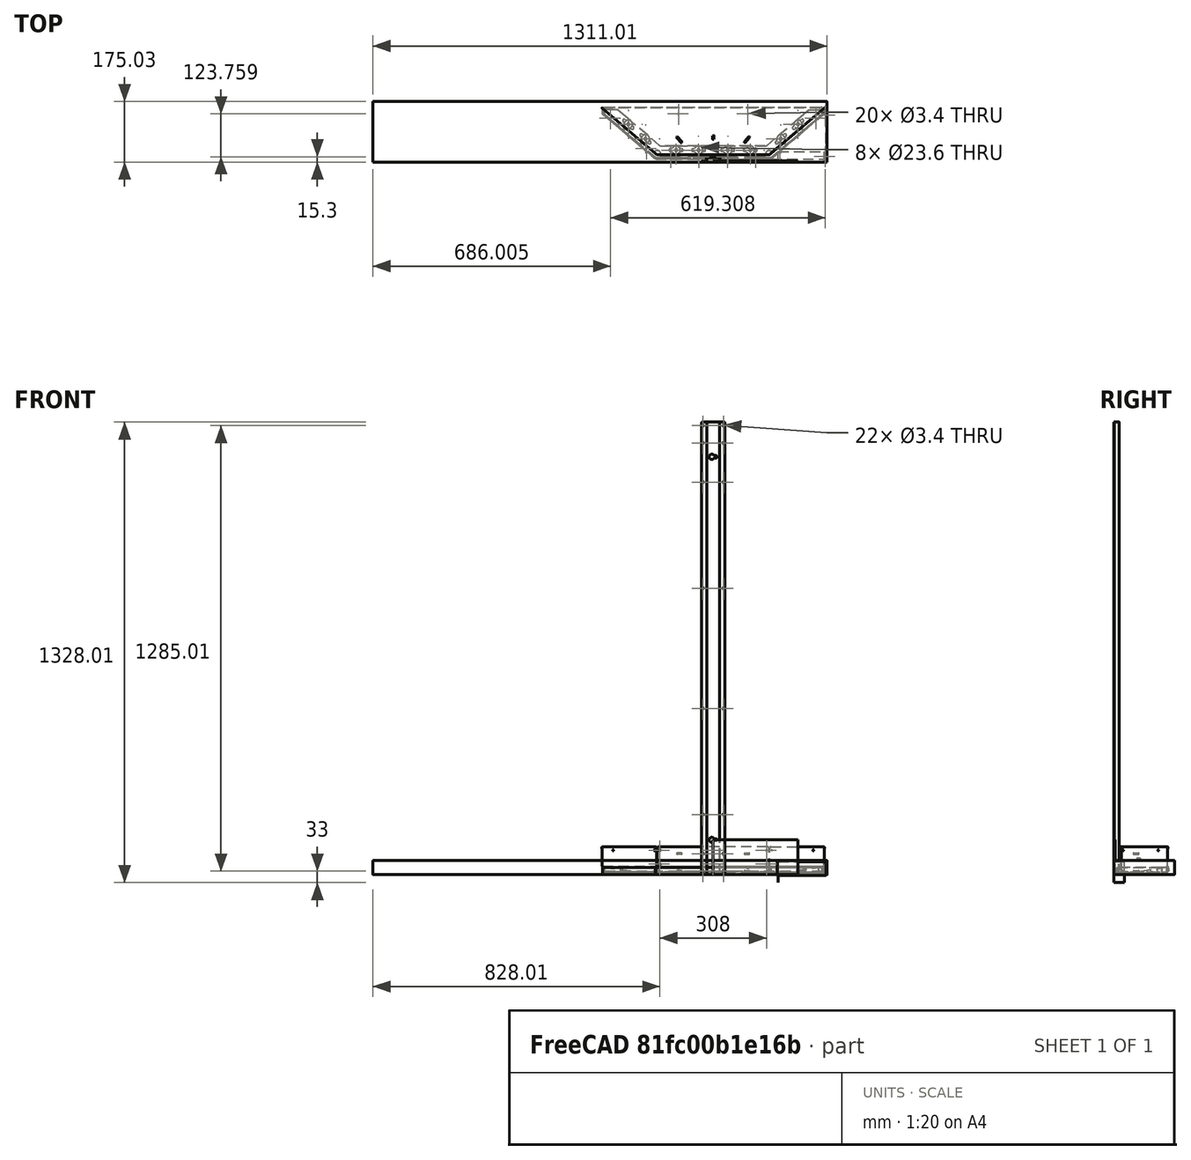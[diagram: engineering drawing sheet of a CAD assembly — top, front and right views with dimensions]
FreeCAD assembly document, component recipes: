
FREECAD ASSEMBLY — COMPONENT RECIPES ("composit_stand7")

This assembly document has 10 components, labeled P0..P9 below (a component is one placed body or linked part). 10 of them carry a construction recipe — the FreeCAD feature program that regenerates the part from scratch, quoted from this document or its linked companion documents; the rest are supplied as boundary geometry only. No exploded tour is included for this assembly.
COMPONENT P0 — recipe-attached ("Body006", modeled in this document).
Construction recipe (the document's own serialized feature program — sketch geometry with constraints, then the solid features built on it; lengths are millimeters unless a unit is written):

FEATURE [PartDesign::SubShapeBinder] Binder011
  BindCopyOnChange = 0
  BindMode = 0
  ClaimChildren = true
  Context = -> Part [Part001.Body005.Boolean003.Body006.Binder011.]
  Fuse = false
  MakeFace = true
  OffsetFill = false
  OffsetIntersection = false
  OffsetJoinType = 0
  OffsetOpenResult = false
  PartialLoad = false
  Relative = false
  Support = -> [Sketch019]
  _Version = 2
FEATURE [PartDesign::FeaturePython] BaseBend004  # WARN: FeaturePython — macro-defined, semantics opaque (R4)
  BendSide = 1
  BendSketch = -> Binder011
  MidPlane = false
  Reverse = true
  length = 10
  radius = 0.1
  thickness = 0.3
FEATURE [PartDesign::Plane] DatumPlane
  AttachmentOffset = pos=(0,0,-326.502) rot=(0,0,1;0rad)
  Length = 220.036
  MapMode = 5
  Placement = pos=(-326.502,0,0) rot=(0.57735,0.57735,0.57735;2.0944rad)
  ResizeMode = 0
  Support = -> [YZ_Plane008]
  Width = 70.0017
  expr: .AttachmentOffset.Base.z = <<faces_bridge>>.Constraints.offset
FEATURE [PartDesign::CoordinateSystem] Local_CS
  AttacherType = Attacher::AttachEngine3D
  AttachmentOffset = pos=(0,0,0) rot=(0,1,0;1.5708rad)
  MapMode = 7
  Placement = pos=(329.002,156.059,0) rot=(0.57735,0.57735,0.57735;2.0944rad)
  Support = -> [Binder011]
FEATURE [Sketcher::SketchObject] Sketch020
  FullyConstrained = true
  MapMode = 5
  Placement = pos=(329.002,156.059,0) rot=(0.57735,0.57735,0.57735;2.0944rad)
  Support = -> [Local_CS]
  expr: Constraints[6] = -<<BaseBend004>>.length
  sketch-geometry (3):
    g0: ArcOfCircle CenterX=5 CenterY=-5 CenterZ=0 NormalX=0 NormalY=0 NormalZ=1 AngleXU=0 Radius=5 StartAngle=3.14159 EndAngle=4.71239
    g1: LineSegment StartX=0 StartY=-5 StartZ=0 EndX=0 EndY=-10 EndZ=0
    g2: LineSegment StartX=0 StartY=-10 StartZ=0 EndX=5 EndY=-10 EndZ=0
  constraints (8):
    c: PointOnObject(g0,g-2)
    c: PointOnObject(g1,g-2)
    c: Coincident(g2,g1)
    c: Horizontal(g2)
    c: Tangent(g2,g0) = -1.5708
    c: Tangent(g1,g0) = -1.5708
    c: DistanceY(g1) = -10
    c: DistanceX(g2,g2) = 5
FEATURE [PartDesign::Pocket] Pocket002
  BaseFeature = -> BaseBend004
  Direction = (-1,0,0)
  Length = 5
  Length2 = 5
  Profile = -> Sketch020
  ReferenceAxis = -> Sketch020 [N_Axis]
  Type = 0
FEATURE [PartDesign::Mirrored] Mirrored002
  BaseFeature = -> Pocket002
  MirrorPlane = -> DatumPlane
  Originals = -> [Pocket002]
FEATURE [PartDesign::Body] Body006
  Group = -> [Binder011,BaseBend004,DatumPlane,Local_CS,Sketch020,Pocket002,Mirrored002]
  Origin = -> Origin008
  Tip = -> Mirrored002
COMPONENT P1 — recipe-attached ("sink2_material_0.30ansi", modeled in this document).
Construction recipe (the document's own serialized feature program — sketch geometry with constraints, then the solid features built on it; lengths are millimeters unless a unit is written):

FEATURE [PartDesign::SubShapeBinder] Binder016
  BindCopyOnChange = 0
  BindMode = 0
  ClaimChildren = true
  Context = -> Body011 [Binder016.]
  Fuse = false
  MakeFace = true
  OffsetFill = false
  OffsetIntersection = false
  OffsetJoinType = 0
  OffsetOpenResult = false
  PartialLoad = false
  Placement = pos=(0,0,0) rot=(1,0,0;1.5708rad)
  Relative = false
  Support = -> [Sketch049]
  _Version = 2
FEATURE [PartDesign::Pad] Pad014
  Direction = (0,-1,2e-16)
  Length = 1
  Length2 = 10
  Placement = pos=(0,0,0) rot=(1,0,0;1.5708rad)
  Profile = -> Binder016
  Reversed = true
  Type = 0
FEATURE [PartDesign::FeaturePython] Bend004  # WARN: FeaturePython — macro-defined, semantics opaque (R4)
  AutoMiter = true
  BaseFeature = -> Pad014
  BendType = 0
  LengthList = [50]
  LengthSpec = 0
  ReliefFactor = 0.7
  UseReliefFactor = false
  angle = 40
  baseObject = -> Pad014 [Edge3]
  bendAList = [40]
  extend1 = 0
  extend2 = 0
  gap1 = 0
  gap2 = 0
  invert = false
  kfactor = 0.5
  length = 50
  maxExtendDist = 5
  minGap = 0.1
  minReliefGap = 1
  miterangle1 = 0
  miterangle2 = 0
  offset = 0
  radius = 1
  reliefType = 0
  reliefd = 1
  reliefw = 0.8
  sketchflip = false
  sketchinvert = false
  unfold = false
FEATURE [Sketcher::SketchObject] Sketch062
  ExternalGeometry = -> [Bend004]
  FullyConstrained = true
  MapMode = 5
  Placement = pos=(0,0.407604,0.34202) rot=(0,0.422618,0.906308;3.14159rad)
  Support = -> [Bend004]
  sketch-geometry (3):
    g0: LineSegment StartX=325.502 StartY=-51.2856 StartZ=0 EndX=-193.217 EndY=-24.1006 EndZ=0
    g1: LineSegment StartX=-193.217 StartY=-24.1006 StartZ=0 EndX=-193.217 EndY=-51.2856 EndZ=0
    g2: LineSegment StartX=-193.217 StartY=-51.2856 StartZ=0 EndX=325.502 EndY=-51.2856 EndZ=0
  constraints (7):
    c: Coincident(g0,g1)
    c: Vertical(g1)
    c: Angle(g0) = 3.08923
    c: Coincident(g0,g-4)
    c: Coincident(g1,g-4)
    c: Coincident(g2,g1)
    c: Coincident(g2,g0)
FEATURE [PartDesign::Pocket] Pocket012
  BaseFeature = -> Bend004
  Direction = (0,-0.766044,-0.642788)
  Length = 5
  Length2 = 5
  Profile = -> Sketch062
  ReferenceAxis = -> Sketch062 [N_Axis]
  Type = 0
FEATURE [PartDesign::FeaturePython] Bend005  # WARN: FeaturePython — macro-defined, semantics opaque (R4)
  AutoMiter = true
  BaseFeature = -> Pocket012
  BendType = 0
  LengthList = [20]
  LengthSpec = 0
  ReliefFactor = 0.7
  UseReliefFactor = false
  angle = 90
  baseObject = -> Pocket012 [Edge10]
  bendAList = [90]
  extend1 = 0
  extend2 = 0
  gap1 = 0
  gap2 = 0
  invert = false
  kfactor = 0.5
  length = 20
  maxExtendDist = 5
  minGap = 0.1
  minReliefGap = 1
  miterangle1 = 0
  miterangle2 = 0
  offset = 0
  radius = 1
  reliefType = 0
  reliefd = 1
  reliefw = 0.8
  sketchflip = false
  sketchinvert = false
  unfold = false
  expr: radius = Bend004.radius
FEATURE [PartDesign::Boolean] Boolean014
  BaseFeature = -> Bend005
  Group = -> [Compound025]
  Type = 1
FEATURE [PartDesign::Fillet] Fillet002
  Base = -> Boolean014 [Edge36,Edge2,Edge8,Edge50]
  BaseFeature = -> Boolean014
  Radius = 11
  SupportTransform = false
  UseAllEdges = false
FEATURE [PartDesign::Body] Body011  label="sink2_material_0.30ansi"
  Group = -> [Binder016,Pad014,Bend004,Sketch062,Pocket012,Bend005,Boolean014,Fillet002]
  Origin = -> Origin014
  Placement = pos=(0,17,0) rot=(0,0,1;0rad)
  Tip = -> Fillet002
  expr: .Placement.Base.y = <<base_sketch>>.Constraints.offset - 3 mm - 1 mm
COMPONENT P2 — recipe-attached ("drain_holder", modeled in this document).
Construction recipe (the document's own serialized feature program — sketch geometry with constraints, then the solid features built on it; lengths are millimeters unless a unit is written):

FEATURE [PartDesign::SubShapeBinder] Binder017
  BindCopyOnChange = 0
  BindMode = 0
  ClaimChildren = true
  Context = -> Body012 [Binder017.]
  Fuse = false
  MakeFace = true
  OffsetFill = false
  OffsetIntersection = false
  OffsetJoinType = 0
  OffsetOpenResult = false
  PartialLoad = false
  Relative = false
  Support = -> [Sketch050]
  _Version = 2
FEATURE [PartDesign::FeaturePython] BaseBend007  # WARN: FeaturePython — macro-defined, semantics opaque (R4)
  BendSide = 0
  BendSketch = -> Binder017
  MidPlane = false
  Reverse = false
  length = 70
  radius = 0.1
  thickness = 0.3
FEATURE [PartDesign::Boolean] Boolean008
  BaseFeature = -> BaseBend007
  Group = -> [Compound018]
  Type = 1
FEATURE [PartDesign::Body] Body012  label="drain_holder"
  Group = -> [Binder017,BaseBend007,Boolean008]
  Origin = -> Origin015
  Placement = pos=(-313,0,-115) rot=(0,0,1;0rad)
  Tip = -> Boolean008
COMPONENT P3 — recipe-attached ("front_shield", modeled in this document).
Construction recipe (the document's own serialized feature program — sketch geometry with constraints, then the solid features built on it; lengths are millimeters unless a unit is written):

FEATURE [PartDesign::SubShapeBinder] Binder020
  BindCopyOnChange = 0
  BindMode = 0
  ClaimChildren = true
  Context = -> Body013 [Binder020.]
  Fuse = false
  MakeFace = true
  OffsetFill = false
  OffsetIntersection = false
  OffsetJoinType = 0
  OffsetOpenResult = false
  PartialLoad = false
  Relative = false
  Support = -> [Sketch057]
  _Version = 2
FEATURE [PartDesign::FeaturePython] BaseBend008  # WARN: FeaturePython — macro-defined, semantics opaque (R4)
  BendSide = 0
  BendSketch = -> Binder020
  MidPlane = false
  Reverse = false
  length = 133
  radius = 0
  thickness = 0.3
  expr: length = <<Properties>>.bottom_extend + 18 mm
FEATURE [PartDesign::Boolean] Boolean009
  BaseFeature = -> BaseBend008
  Group = -> [Compound017]
  Type = 1
FEATURE [PartDesign::Body] Body013  label="front_shield"
  Group = -> [Binder020,BaseBend008,Boolean009]
  Origin = -> Origin016
  Placement = pos=(0,154.059,-115) rot=(0,0,1;0rad)
  Tip = -> Boolean009
  expr: Placement = <<front_shield_placement>>.Placement
COMPONENT P4 — recipe-attached ("led_holder", modeled in this document).
Construction recipe (the document's own serialized feature program — sketch geometry with constraints, then the solid features built on it; lengths are millimeters unless a unit is written):

FEATURE [PartDesign::SubShapeBinder] Binder023
  BindCopyOnChange = 0
  BindMode = 0
  ClaimChildren = true
  Context = -> Body015 [Binder023.]
  Fuse = false
  MakeFace = true
  OffsetFill = false
  OffsetIntersection = false
  OffsetJoinType = 0
  OffsetOpenResult = false
  PartialLoad = false
  Relative = true
  Support = -> [Sketch060]
  _Version = 2
FEATURE [PartDesign::SubShapeBinder] Binder024
  BindCopyOnChange = 0
  BindMode = 0
  ClaimChildren = true
  Context = -> Body015 [Binder024.]
  Fuse = false
  MakeFace = true
  OffsetFill = false
  OffsetIntersection = false
  OffsetJoinType = 0
  OffsetOpenResult = false
  PartialLoad = false
  Relative = true
  Support = -> [Sketch010]
  _Version = 2
  expr: Support = <<top_base_sketch>>._self
FEATURE [Sketcher::SketchObject] Sketch061  label="led_holder_base_sketch"
  ExternalGeometry = -> [Binder024,Binder023]
  FullyConstrained = true
  MapMode = 5
  Placement = pos=(0,0,0) rot=(0.57735,0.57735,0.57735;2.0944rad)
  Support = -> [YZ_Plane018]
  sketch-geometry (16):
    g0: LineSegment StartX=126.541 StartY=3 StartZ=0 EndX=151.541 EndY=3 EndZ=0
    g1: LineSegment StartX=151.541 StartY=3 StartZ=0 EndX=155.272 EndY=24.1563 EndZ=0
    g2: LineSegment StartX=155.272 StartY=24.1563 StartZ=0 EndX=183.226 EndY=19.2272 EndZ=0
    g3: LineSegment StartX=183.226 StartY=19.2272 StartZ=0 EndX=183.226 EndY=24.3043 EndZ=0
    g4: LineSegment StartX=183.226 StartY=24.3043 StartZ=0 EndX=155.155 EndY=29.254 EndZ=0
    g5: LineSegment StartX=150.522 StartY=26.0094 StartZ=0 EndX=147.929 EndY=11.3054 EndZ=0
    g6: LineSegment StartX=143.99 StartY=8 StartZ=0 EndX=126.541 EndY=8 EndZ=0
    g7: LineSegment StartX=126.541 StartY=8 StartZ=0 EndX=126.541 EndY=3 EndZ=0
    g8: ArcOfCircle CenterX=143.99 CenterY=12 CenterZ=0 NormalX=0 NormalY=0 NormalZ=1 AngleXU=0 Radius=4 StartAngle=4.71239 EndAngle=6.10865
    g9: GeomPoint X=147.346 Y=8 Z=0
    g10: LineSegment StartX=151.541 StartY=0 StartZ=0 EndX=151.541 EndY=3 EndZ=0
    g11: LineSegment StartX=151.541 StartY=3 StartZ=0 EndX=154.496 EndY=2.47906 EndZ=0
    g12: ArcOfCircle CenterX=154.461 CenterY=25.3148 CenterZ=0 NormalX=0 NormalY=0 NormalZ=1 AngleXU=0 Radius=4 StartAngle=1.39626 EndAngle=2.96706
    g13: GeomPoint X=151.216 Y=29.9486 Z=0
    g14: LineSegment StartX=155.272 StartY=24.1563 StartZ=0 EndX=151.216 EndY=29.9486 EndZ=0
    g15: LineSegment StartX=151.541 StartY=3 StartZ=0 EndX=146.617 EndY=3.86824 EndZ=0
  constraints (44):
    c: Horizontal(g0)
    c: Coincident(g0,g1)
    c: Coincident(g1,g2)
    c: Coincident(g2,g3)
    c: Coincident(g3,g4)
    c: Horizontal(g6)
    c: Coincident(g6,g7)
    c: Coincident(g7,g0)
    c: Vertical(g7)
    c: PointOnObject(g9,g5)
    c: PointOnObject(g9,g6)
    c: Tangent(g5,g8) = 1.5708
    c: Tangent(g6,g8) = 1.5708
    c: PointOnObject(g10,g-1)
    c: Coincident(g10,g0)
    c: Vertical(g10)
    c: Coincident(g10,g11)
    c: PointOnObject(g11,g-3)
    c: Perpendicular(g-3,g11)
    c: Perpendicular(g1,g11)
    c: Equal(g10,g11)
    c: DistanceY(g10,g10) = 3
    c: Perpendicular(g-3,g2)
    c: PointOnObject(g-3,g2)
    c: DistanceX(g-3,g3) = 25
    c: PointOnObject(g13,g4)
    c: PointOnObject(g13,g5)
    c: Tangent(g4,g12) = -1.5708
    c: Tangent(g5,g12) = -1.5708
    c: Coincident(g14,g1)
    c: Coincident(g14,g13)
    c: PointOnObject(g12,g14)
    c: Parallel(g5,g1)
    c: Coincident(g15,g0)
    c: PointOnObject(g15,g5)
    c: Perpendicular(g5,g15)
    c: Distance(g15) = 5
    c: Equal(g8,g12)
    c: Equal(g15,g7)
    c: Radius(g8) = 4
    c: DistanceX(g0,g0) = 25
    c: Parallel(g2,g4)
    c: Vertical(g3)
    c: DistanceX(g2) = 183.226  'total_length'
FEATURE [PartDesign::Pad] Pad016
  Direction = (1,0,0)
  Length = 15
  Length2 = 10
  Midplane = true
  Placement = pos=(0,0,0) rot=(0.57735,0.57735,0.57735;2.0944rad)
  Profile = -> Sketch061
  ReferenceAxis = -> Sketch061 [N_Axis]
  Type = 0
FEATURE [PartDesign::Boolean] Boolean013
  BaseFeature = -> Pad016
  Group = -> [Compound024]
  Type = 1
FEATURE [PartDesign::Body] Body015  label="led_holder"
  Group = -> [Sketch061,Binder023,Binder024,Pad016,Boolean013]
  Origin = -> Origin018
  Tip = -> Boolean013
COMPONENT P5 — recipe-attached ("module", modeled in this document).
Construction recipe (the document's own serialized feature program — sketch geometry with constraints, then the solid features built on it; lengths are millimeters unless a unit is written):

FEATURE [PartDesign::SubShapeBinder] Binder
  BindCopyOnChange = 0
  BindMode = 0
  ClaimChildren = true
  Context = -> Body [Binder.]
  Fuse = false
  MakeFace = true
  OffsetFill = false
  OffsetIntersection = false
  OffsetJoinType = 0
  OffsetOpenResult = false
  PartialLoad = false
  Placement = pos=(0,0,-115) rot=(0,0,1;0rad)
  Relative = false
  Support = -> [Connect002]
  _Version = 2
  expr: .Placement.Base.z = -<<Properties>>.bottom_extend
FEATURE [PartDesign::FeaturePython] BaseBend  # WARN: FeaturePython — macro-defined, semantics opaque (R4)
  BendSide = 0
  BendSketch = -> Binder
  MidPlane = false
  Reverse = false
  length = 870
  radius = 0.1
  thickness = 0.3
  expr: length = <<Properties>>.face_height - .BendSketch.Placement.Base.z * 1 mm
FEATURE [PartDesign::FeaturePython] Extend  # WARN: FeaturePython — macro-defined, semantics opaque (R4)
  BaseFeature = -> BaseBend
  Offset = 0.02
  Refine = true
  UseSubtraction = false
  baseObject = -> BaseBend [Face1]
  gap1 = 0
  gap2 = 0
  length = 0
FEATURE [PartDesign::FeaturePython] Bend  # WARN: FeaturePython — macro-defined, semantics opaque (R4)
  AutoMiter = false
  BaseFeature = -> Extend
  BendType = 0
  LengthList = [0.1]
  LengthSpec = 0
  ReliefFactor = 0.7
  UseReliefFactor = false
  angle = 90
  baseObject = -> Extend [Edge17,Edge49,Edge199,Edge78,Edge108,Edge203,Edge138,Edge171]
  bendAList = [90]
  extend1 = 0
  extend2 = 0
  gap1 = 0
  gap2 = 0
  invert = false
  kfactor = 0.5
  length = 0.1
  maxExtendDist = 5
  minGap = 0.1
  minReliefGap = 1
  miterangle1 = 0
  miterangle2 = 0
  offset = 0
  radius = 0.1
  reliefType = 0
  reliefd = 1
  reliefw = 0.8
  sketchflip = false
  sketchinvert = false
  unfold = false
  expr: radius = BaseBend.radius
FEATURE [PartDesign::SubShapeBinder] Binder001
  BindCopyOnChange = 0
  BindMode = 0
  ClaimChildren = true
  Context = -> Body [Binder001.]
  Fuse = false
  MakeFace = true
  OffsetFill = false
  OffsetIntersection = false
  OffsetJoinType = 0
  OffsetOpenResult = false
  PartialLoad = false
  Placement = pos=(0,0,755.1) rot=(0,0,1;0rad)
  Relative = false
  Support = -> [Compound004]
  _Version = 2
  expr: .Placement.Base.z = <<Properties>>.face_height + <<BaseBend>>.radius
FEATURE [PartDesign::Pad] Pad
  BaseFeature = -> Bend
  Direction = (0,0,1)
  Length = 0.3
  Length2 = 10
  Profile = -> Binder001
  Type = 0
  expr: Length = <<BaseBend>>.thickness
FEATURE [PartDesign::SubShapeBinder] Binder018
  BindCopyOnChange = 0
  BindMode = 0
  ClaimChildren = false
  Context = -> Body [Binder018.]
  Fuse = false
  MakeFace = true
  OffsetFill = false
  OffsetIntersection = false
  OffsetJoinType = 0
  OffsetOpenResult = false
  PartialLoad = false
  Relative = true
  Support = -> [Sketch]
  _Version = 2
  expr: Support = <<base_sketch>>._self
FEATURE [PartDesign::SubShapeBinder] Binder019
  BindCopyOnChange = 0
  BindMode = 0
  ClaimChildren = false
  Context = -> Body [Binder019.]
  Fuse = false
  MakeFace = true
  OffsetFill = false
  OffsetIntersection = false
  OffsetJoinType = 0
  OffsetOpenResult = false
  PartialLoad = false
  Relative = true
  Support = -> [Sketch053]
  _Version = 2
  expr: Support = <<face_cut>>._self
FEATURE [Sketcher::SketchObject] Sketch054
  AttachmentOffset = pos=(0,0,0) rot=(0,-1,0;1.5708rad)
  ExternalGeometry = -> [Binder019]
  FullyConstrained = true
  MapMode = 7
  Placement = pos=(162.217,21,0) rot=(0.251276,-0.68442,-0.68442;2.64923rad)
  Support = -> [Binder018]
  expr: Constraints[8] = 180 deg - 6 deg
  sketch-geometry (7):
    g0: ArcOfCircle CenterX=-0.3 CenterY=0 CenterZ=0 NormalX=0 NormalY=0 NormalZ=1 AngleXU=0 Radius=15 StartAngle=1.5708 EndAngle=2.78257
    g1: ArcOfCircle CenterX=-19.0248 CenterY=7.02713 CenterZ=0 NormalX=0 NormalY=0 NormalZ=1 AngleXU=0 Radius=5 StartAngle=4.60767 EndAngle=5.92417
    g2: LineSegment StartX=-19.5475 StartY=2.05452 StartZ=0 EndX=-77.2728 EndY=8.12169 EndZ=0
    g3: LineSegment StartX=-77.2728 StartY=8.12169 StartZ=0 EndX=-77.2728 EndY=0 EndZ=0
    g4: LineSegment StartX=-77.2728 StartY=0 StartZ=0 EndX=0.17 EndY=0 EndZ=0
    g5: LineSegment StartX=0.17 StartY=15 StartZ=0 EndX=-0.3 EndY=15 EndZ=0
    g6: LineSegment StartX=0.17 StartY=0 StartZ=0 EndX=0.17 EndY=15 EndZ=0
  constraints (19):
    c: PointOnObject(g0,g-1)
    c: Tangent(g1,g2) = 1.5708
    c: Coincident(g2,g3)
    c: Vertical(g3)
    c: Coincident(g3,g4)
    c: Horizontal(g5)
    c: Tangent(g5,g0) = -1.5708
    c: Tangent(g1,g0) = 1.5708
    c: Angle(g2) = 3.03687
    c: Radius(g0) = 15
    c: Radius(g1) = 5
    c: Coincident(g3,g-3)
    c: DistanceX(g-2,g0) = -0.3
    c: PointOnObject(g4,g-1)
    c: Coincident(g6,g4)
    c: Coincident(g6,g5)
    c: Vertical(g6)
    c: DistanceX(g4) = 0.17
    c: PointOnObject(g-1,g2)
FEATURE [Sketcher::SketchObject] Sketch055
  AttachmentOffset = pos=(0,0,0) rot=(0,-1,0;1.5708rad)
  FullyConstrained = true
  MapMode = 7
  Placement = pos=(162.217,21,0) rot=(0,-0.707107,-0.707107;3.14159rad)
  Support = -> [Binder018]
  sketch-geometry (5):
    g0: LineSegment StartX=0.3 StartY=15 StartZ=0 EndX=-0.17 EndY=15 EndZ=0
    g1: LineSegment StartX=-0.17 StartY=0 StartZ=0 EndX=19.6649 EndY=0 EndZ=0
    g2: ArcOfCircle CenterX=0.3 CenterY=0 CenterZ=0 NormalX=0 NormalY=0 NormalZ=1 AngleXU=0 Radius=15 StartAngle=0.25268 EndAngle=1.5708
    g3: ArcOfCircle CenterX=19.6649 CenterY=5 CenterZ=0 NormalX=0 NormalY=0 NormalZ=1 AngleXU=0 Radius=5 StartAngle=3.39427 EndAngle=4.71239
    g4: LineSegment StartX=-0.17 StartY=15 StartZ=0 EndX=-0.17 EndY=0 EndZ=0
  constraints (14):
    c: PointOnObject(g1,g-1)
    c: Tangent(g2,g0) = -1.5708
    c: Horizontal(g0)
    c: Radius(g2) = 15
    c: Tangent(g3,g2) = 1.5708
    c: DistanceX(g0) = 0.3
    c: PointOnObject(g2,g1)
    c: Radius(g3) = 5
    c: Tangent(g3,g1) = -1.5708
    c: PointOnObject(g1,g-1)
    c: DistanceX(g1) = -0.17
    c: Coincident(g4,g0)
    c: Coincident(g4,g1)
    c: Vertical(g4)
FEATURE [PartDesign::Pocket] Pocket010
  BaseFeature = -> Pad
  Direction = (0.647059,-0.76244,-1e-16)
  Length = 5
  Length2 = 5
  Midplane = true
  Profile = -> Sketch054
  ReferenceAxis = -> Sketch054 [N_Axis]
  Refine = true
  Type = 0
FEATURE [PartDesign::Pocket] Pocket011
  BaseFeature = -> Pocket010
  Direction = (2e-16,-1,0)
  Length = 5
  Length2 = 5
  Midplane = true
  Profile = -> Sketch055
  ReferenceAxis = -> Sketch055 [N_Axis]
  Refine = true
  Type = 0
FEATURE [Sketcher::SketchObject] Sketch056
  ExternalGeometry = -> [Binder018]
  FullyConstrained = true
  MapMode = 1
  Placement = pos=(162.217,21,0) rot=(0,0,1;0rad)
  Support = -> [Binder018]
  sketch-geometry (4):
    g0: ArcOfCircle CenterX=-0.0367138 CenterY=0.1 CenterZ=0 NormalX=0 NormalY=0 NormalZ=1 AngleXU=0 Radius=0.1 StartAngle=4.71239 EndAngle=5.41611
    g1: LineSegment StartX=-0.0367138 StartY=0.1 StartZ=0 EndX=-0.0367138 EndY=-3.0958 EndZ=0
    g2: LineSegment StartX=-0.0367138 StartY=-3.0958 StartZ=0 EndX=2.03115 EndY=-2.3366 EndZ=0
    g3: LineSegment StartX=2.03115 StartY=-2.3366 StartZ=0 EndX=-0.0367138 EndY=0.1 EndZ=0
  constraints (11):
    c: Radius(g0) = 0.1
    c: Tangent(g0,g-3) = -1.5708
    c: Tangent(g0,g-1) = -1.5708
    c: Coincident(g1,g0)
    c: Vertical(g1)
    c: Coincident(g1,g2)
    c: Coincident(g2,g3)
    c: Coincident(g3,g1)
    c: PointOnObject(g0,g3)
    c: Equal(g1,g3)
    c: Distance(g1,g2) = 3
FEATURE [PartDesign::Plane] DatumPlane003
  AttachmentOffset = pos=(0,0,-326.502) rot=(0,0,1;0rad)
  Length = 258.015
  MapMode = 5
  Placement = pos=(-326.502,0,0) rot=(0.57735,0.57735,0.57735;2.0944rad)
  ResizeMode = 0
  Support = -> [YZ_Plane]
  Width = 949.356
  expr: .AttachmentOffset.Base.z = <<faces_bridge>>.Constraints.offset
FEATURE [PartDesign::Mirrored] Mirrored007
  MirrorPlane = -> YZ_Plane
FEATURE [PartDesign::Mirrored] Mirrored008
  MirrorPlane = -> DatumPlane003
FEATURE [PartDesign::MultiTransform] MultiTransform001
  BaseFeature = -> Pocket011
  Originals = -> [Pocket010,Pocket011]
  Transformations = -> [Mirrored007,Mirrored008]
FEATURE [PartDesign::Boolean] Boolean
  BaseFeature = -> MultiTransform001
  Group = -> [Compound]
  Refine = true
  Type = 1
FEATURE [PartDesign::Body] Body  label="face_material_0.30ansi"
  Group = -> [Binder,BaseBend,Extend,Bend,Binder001,Pad,Binder018,Sketch054,Binder019,Sketch055,Pocket010,Pocket011,Sketch056,DatumPlane003,MultiTransform001,Mirrored007,Mirrored008,Boolean]
  Origin = -> Origin
  Tip = -> Boolean
COMPONENT P6 — recipe-attached ("top", modeled in this document).
Construction recipe (the document's own serialized feature program — sketch geometry with constraints, then the solid features built on it; lengths are millimeters unless a unit is written):

FEATURE [PartDesign::FeaturePython] BaseBend001  # WARN: FeaturePython — macro-defined, semantics opaque (R4)
  BendSide = 1
  BendSketch = -> Sketch010
  MidPlane = true
  Reverse = false
  length = 638.005
  radius = 0.1
  thickness = 0.3
  expr: length = <<base_sketch>>.Constraints.width * 2
FEATURE [PartDesign::SubShapeBinder] Binder002
  BindCopyOnChange = 0
  BindMode = 0
  ClaimChildren = true
  Context = -> Part [Body002.Binder002.]
  Fuse = false
  MakeFace = true
  OffsetFill = false
  OffsetIntersection = false
  OffsetJoinType = 0
  OffsetOpenResult = false
  PartialLoad = false
  Relative = false
  Support = -> [Connect004]
  _Version = 2
FEATURE [PartDesign::Pocket] Pocket
  BaseFeature = -> BaseBend001
  Direction = (0,0,-1)
  Length = 5
  Length2 = 5
  Midplane = true
  Profile = -> Binder002
  Refine = true
  Type = 1
FEATURE [PartDesign::FeaturePython] Bend001  # WARN: FeaturePython — macro-defined, semantics opaque (R4)
  AutoMiter = false
  BaseFeature = -> Pocket
  BendType = 1
  LengthList = [20]
  LengthSpec = 0
  ReliefFactor = 0.7
  UseReliefFactor = false
  angle = 90
  baseObject = -> Pocket [Edge27,Edge29,Edge32,Edge33,Edge26]
  bendAList = [90]
  extend1 = 0
  extend2 = 0
  gap1 = 0
  gap2 = 0
  invert = false
  kfactor = 0.5
  length = 20
  maxExtendDist = 5
  minGap = 0.1
  minReliefGap = 1
  miterangle1 = 0
  miterangle2 = 0
  offset = 0
  radius = 0.1
  reliefType = 0
  reliefd = 1
  reliefw = 0.8
  sketchflip = false
  sketchinvert = false
  unfold = false
  expr: radius = BaseBend001.radius
FEATURE [PartDesign::SubShapeBinder] Binder003
  BindCopyOnChange = 0
  BindMode = 0
  ClaimChildren = false
  Context = -> Part [Body002.Binder003.]
  Fuse = false
  MakeFace = true
  OffsetFill = false
  OffsetIntersection = false
  OffsetJoinType = 0
  OffsetOpenResult = false
  PartialLoad = false
  Relative = true
  Support = -> [Sketch,Sketch011]
  _Version = 2
  expr: Support = list(<<top_cut>>._self; <<base_sketch>>._self)
FEATURE [PartDesign::Pocket] Pocket001
  BaseFeature = -> Bend001
  Direction = (0,0,-1)
  Length = 5
  Length2 = 5
  Profile = -> Sketch013
  ReferenceAxis = -> Sketch013 [N_Axis]
  Reversed = true
  Type = 1
FEATURE [PartDesign::Mirrored] Mirrored
  BaseFeature = -> Pocket001
  MirrorPlane = -> Sketch013 [V_Axis]
  Originals = -> [Pocket001]
FEATURE [PartDesign::SubShapeBinder] Binder006
  BindCopyOnChange = 0
  BindMode = 0
  ClaimChildren = false
  Context = -> Part [Body003.Binder006.]
  Fuse = false
  MakeFace = true
  OffsetFill = false
  OffsetIntersection = false
  OffsetJoinType = 0
  OffsetOpenResult = false
  PartialLoad = false
  Relative = false
  Support = -> [Sketch011]
  _Version = 2
FEATURE [PartDesign::SubShapeBinder] Binder008
  BindCopyOnChange = 0
  BindMode = 0
  ClaimChildren = false
  Context = -> Part [Body003.Binder008.]
  Fuse = false
  MakeFace = true
  OffsetFill = false
  OffsetIntersection = false
  OffsetJoinType = 0
  OffsetOpenResult = false
  PartialLoad = false
  Relative = true
  Support = -> [Sketch]
  _Version = 2
  expr: Support = <<base_sketch>>._self
FEATURE [Sketcher::SketchObject] Sketch016
  ExternalGeometry = -> [Binder006,Binder008]
  FullyConstrained = true
  MapMode = 5
  Support = -> [XY_Plane004]
  expr: Constraints[45] = <<base_sketch>>.Constraints.offset + LinearArray002.Placement.Base.y + 11.8 mm
  sketch-geometry (17):
    g0: LineSegment StartX=166.623 StartY=9 StartZ=0 EndX=167.462 EndY=9.71268 EndZ=0
    g1: LineSegment StartX=167.462 StartY=9.71268 StartZ=0 EndX=165.521 EndY=12 EndZ=0
    g2: LineSegment StartX=165.521 StartY=12 StartZ=0 EndX=165.521 EndY=9 EndZ=0
    g3: LineSegment StartX=165.521 StartY=9 StartZ=0 EndX=166.623 EndY=9 EndZ=0
    g4: LineSegment StartX=0 StartY=12 StartZ=0 EndX=165.521 EndY=12 EndZ=0
    g5: LineSegment StartX=165.521 StartY=12 StartZ=0 EndX=312.059 EndY=136.362 EndZ=0
    g6: LineSegment StartX=149.757 StartY=46.6 StartZ=0 EndX=0 EndY=46.6 EndZ=0
    g7: LineSegment StartX=0 StartY=46.6 StartZ=0 EndX=0 EndY=12 EndZ=0
    g8: ArcOfCircle CenterX=149.757 CenterY=54.9388 CenterZ=0 NormalX=0 NormalY=0 NormalZ=1 AngleXU=0 Radius=8.33877 StartAngle=4.71239 EndAngle=5.41611
    g9: GeomPoint X=152.818 Y=46.6 Z=0
    g10: LineSegment StartX=152.818 StartY=46.6 StartZ=0 EndX=152.818 EndY=9 EndZ=0
    g11: LineSegment StartX=155.152 StartY=48.581 StartZ=0 EndX=275.904 EndY=151.059 EndZ=0
    g12: LineSegment StartX=152.818 StartY=46.6 StartZ=0 EndX=177.148 EndY=17.9322 EndZ=0
    g13: LineSegment StartX=275.904 StartY=151.059 StartZ=0 EndX=306.664 EndY=151.059 EndZ=0
    g14: ArcOfCircle CenterX=306.664 CenterY=142.72 CenterZ=0 NormalX=0 NormalY=0 NormalZ=1 AngleXU=0 Radius=8.33877 StartAngle=5.41611 EndAngle=7.85398
    g15: GeomPoint X=329.377 Y=151.059 Z=0
    g16: LineSegment StartX=315.002 StartY=134.925 StartZ=0 EndX=315.002 EndY=150.664 EndZ=0
  constraints (46):
    c: Coincident(g-4,g0)
    c: PointOnObject(g0,g-3)
    c: Coincident(g0,g1)
    c: Coincident(g1,g2)
    c: PointOnObject(g2,g-4)
    c: Vertical(g2)
    c: Coincident(g2,g3)
    c: Coincident(g3,g0)
    c: Perpendicular(g1,g0)
    c: Equal(g1,g2)
    c: PointOnObject(g4,g-2)
    c: Coincident(g4,g1)
    c: Coincident(g5,g4)
    c: PointOnObject(g6,g-2)
    c: Coincident(g7,g6)
    c: Coincident(g7,g4)
    c: Horizontal(g4)
    c: Perpendicular(g5,g1)
    c: PointOnObject(g9,g6)
    c: Tangent(g6,g8) = 1.5708
    c: Coincident(g10,g9)
    c: Vertical(g10)
    c: PointOnObject(g10,g-4)
    c: DistanceY(g2,g2) = 3
    c: PointOnObject(g9,g11)
    c: Tangent(g11,g8) = -1.5708
    c: Parallel(g11,g5)
    c: Perpendicular(g7,g6)
    c: Coincident(g12,g9)
    c: PointOnObject(g12,g-3)
    c: Perpendicular(g-3,g12)
    c: Horizontal(g13)
    c: DistanceY(g15,g-5) = 3
    c: Coincident(g13,g11)
    c: PointOnObject(g15,g5)
    c: PointOnObject(g15,g13)
    c: Tangent(g5,g14) = -1.5708
    c: Tangent(g13,g14) = 1.5708
    c: PointOnObject(g16,g-3)
    c: PointOnObject(g16,g-5)
    c: Vertical(g16)
    c: Distance(g-3,g16) = 4
    c: Tangent(g16,g14)
    c: Equal(g10,g12)
    c: Equal(g8,g14)
    c: DistanceY(g6) = 46.6
FEATURE [PartDesign::Pad] Pad001
  Direction = (0,0,1)
  Length = 5
  Length2 = 10
  Profile = -> Sketch016
  ReferenceAxis = -> Sketch016 [N_Axis]
  Type = 0
FEATURE [PartDesign::Mirrored] Mirrored001
  BaseFeature = -> Pad001
  MirrorPlane = -> Sketch016 [V_Axis]
  Originals = -> [Pad001]
  Refine = true
FEATURE [PartDesign::SubShapeBinder] Binder009
  BindCopyOnChange = 0
  BindMode = 0
  ClaimChildren = false
  Context = -> Part [Body004.Binder009.]
  Fuse = false
  MakeFace = true
  OffsetFill = false
  OffsetIntersection = false
  OffsetJoinType = 0
  OffsetOpenResult = false
  PartialLoad = false
  Relative = false
  Support = -> [Sketch002,Sketch011]
  _Version = 2
  expr: Support = list(<<wall>>._self; <<top_cut>>._self)
FEATURE [Sketcher::SketchObject] Sketch017
  ExternalGeometry = -> [Binder009]
  FullyConstrained = true
  MapMode = 5
  Support = -> [XY_Plane005]
  sketch-geometry (4):
    g0: LineSegment StartX=166.623 StartY=9 StartZ=0 EndX=326.002 EndY=9 EndZ=0
    g1: LineSegment StartX=326.002 StartY=9 StartZ=0 EndX=326.002 EndY=138.32 EndZ=0
    g2: LineSegment StartX=326.002 StartY=138.32 StartZ=0 EndX=319.002 EndY=138.32 EndZ=0
    g3: LineSegment StartX=319.002 StartY=138.32 StartZ=0 EndX=166.623 EndY=9 EndZ=0
  constraints (10):
    c: Horizontal(g0)
    c: Coincident(g0,g1)
    c: Vertical(g1)
    c: Coincident(g1,g2)
    c: Horizontal(g2)
    c: Coincident(g2,g3)
    c: Coincident(g3,g0)
    c: DistanceX(g0,g-3) = 3
    c: Coincident(g2,g-4)
    c: Coincident(g0,g-4)
FEATURE [PartDesign::FeaturePython] BaseBend002  # WARN: FeaturePython — macro-defined, semantics opaque (R4)
  BendSide = 0
  BendSketch = -> Sketch017
  MidPlane = false
  Reverse = false
  length = 100
  radius = 0.1
  thickness = 0.3
FEATURE [PartDesign::FeaturePython] Bend002  # WARN: FeaturePython — macro-defined, semantics opaque (R4)
  AutoMiter = true
  BaseFeature = -> BaseBend002
  BendType = 1
  LengthList = [20]
  LengthSpec = 0
  ReliefFactor = 0.7
  UseReliefFactor = false
  angle = 90
  baseObject = -> BaseBend002 [Edge11]
  bendAList = [90]
  extend1 = 0
  extend2 = 0
  gap1 = 0
  gap2 = 0
  invert = false
  kfactor = 0.5
  length = 20
  maxExtendDist = 5
  minGap = 0.1
  minReliefGap = 1
  miterangle1 = 0
  miterangle2 = 0
  offset = 0
  radius = 0.1
  reliefType = 0
  reliefd = 1
  reliefw = 0.8
  sketchflip = false
  sketchinvert = false
  unfold = false
  expr: radius = BaseBend.radius
FEATURE [PartDesign::Boolean] Boolean012
  BaseFeature = -> Bend002
  Group = -> [Compound023]
  Type = 1
FEATURE [PartDesign::Body] Body004  label="top_supplement_material_0.30ansi"
  Group = -> [Binder009,Sketch017,BaseBend002,Bend002,Boolean012]
  Origin = -> Origin005
  Tip = -> Boolean012
FEATURE [PartDesign::Boolean] Boolean001
  BaseFeature = -> Mirrored
  Group = -> [Compound007]
  Type = 1
FEATURE [PartDesign::Body] Body002  label="top_material_0.30ansi"
  Group = -> [BaseBend001,Binder002,Pocket,Bend001,Pocket001,Mirrored,Boolean001,Binder003]
  Origin = -> Origin003
  Tip = -> Boolean001
FEATURE [PartDesign::Boolean] Boolean002
  BaseFeature = -> Mirrored001
  Group = -> [Compound009]
  Type = 1
FEATURE [PartDesign::Body] Body003  label="top_dropper_fix"
  Group = -> [Binder006,Sketch016,Pad001,Mirrored001,Boolean002,Binder008]
  Origin = -> Origin004
  Placement = pos=(0,0,3) rot=(0,0,1;0rad)
  Tip = -> Boolean002
COMPONENT P7 — recipe-attached ("sink", modeled in this document).
Construction recipe (the document's own serialized feature program — sketch geometry with constraints, then the solid features built on it; lengths are millimeters unless a unit is written):

FEATURE [PartDesign::Body] Body008  label="sink_hand"
  Origin = -> Origin011
FEATURE [Part::Part2DObjectPython] Line001  # Draft 2D object (typed FeaturePython)
  Area = 0
  ChamferSize = 0
  Closed = false
  End = (-162.217,21,-5e-16)
  FilletRadius = 0
  Length = 324.434
  MakeFace = false
  Placement = pos=(0,0,0) rot=(-0.14785,0.816318,0.55836;2.18251rad)
  Points = (2) [(-81.9646,-95.0022,104.937),(93.1832,114.943,-69.7159)]
  Start = (162.217,21,-5e-16)
  Subdivisions = 0
  expr: .End.x = -.Start.x
  expr: .End.y = .Start.y
  expr: .End.z = .Start.z
  expr: Start = <<Line>>.Start
FEATURE [PartDesign::SubShapeBinder] Binder013
  BindCopyOnChange = 0
  BindMode = 0
  ClaimChildren = false
  Context = -> Part002 [Body007.Binder013.]
  Fuse = false
  MakeFace = true
  OffsetFill = false
  OffsetIntersection = false
  OffsetJoinType = 0
  OffsetOpenResult = false
  PartialLoad = false
  Relative = false
  Support = -> [Sketch]
  _Version = 2
  expr: Support = <<base_sketch>>._self
FEATURE [Part::Part2DObjectPython] Line  # Draft 2D object (typed FeaturePython)
  Angle = 5.55506
  AngleYZ = 8.54811
  Area = 0
  ChamferSize = 0
  Closed = false
  End = (319.002,154.059,20)
  FilletRadius = 0
  Length = 206.607
  MakeFace = false
  MapMode = 1
  Placement = pos=(162.217,21,0) rot=(-0.14785,0.816318,0.55836;2.18251rad)
  Points = (2) [(1.42109e-14,1.42109e-14,-2.84217e-14),(-65.0656,-26.3536,194.315)]
  Start = (162.217,21,-5e-16)
  Subdivisions = 0
  Support = -> [Binder013]
  expr: Angle = asin((.End.z - .Start.z) / Length)
  expr: AngleYZ = asin((.End.z - .Start.z) / hypot(.End.y - .Start.y; .End.z - .Start.z))
  expr: End = <<DatumPoint>>.Placement.Base
FEATURE [PartDesign::Point] DatumPoint
  AttacherType = Attacher::AttachEnginePoint
  AttachmentOffset = pos=(0,0,20) rot=(0,0,1;0rad)
  MapMode = 39
  Placement = pos=(319.002,154.059,20) rot=(0,0,1;0rad)
  Support = -> [Binder013]
FEATURE [PartDesign::CoordinateSystem] Local_CS001
  AttacherType = Attacher::AttachEngine3D
  AttachmentOffset = pos=(0,21,0) rot=(1,0,0;0.149193rad)
  MapMode = 5
  Placement = pos=(0,21,0) rot=(1,0,0;0.149193rad)
  Support = -> [XY_Plane010]
  expr: .AttachmentOffset.Base.y = <<Line>>.Start.y
  expr: .AttachmentOffset.Rotation.Angle = <<Line>>.AngleYZ
FEATURE [Part::Part2DObjectPython] Line002  # Draft 2D object (typed FeaturePython)
  Area = 0
  ChamferSize = 0
  Closed = false
  End = (0,154.059,20)
  FilletRadius = 0
  Length = 134.553
  MakeFace = true
  Placement = pos=(-8.82408,2.54769,28.5595) rot=(0.548521,0.511664,0.661305;1.81276rad)
  Points = (2) [(20.7889,-28.2166,-2.37515),(151.568,2.1228,-11.3743)]
  Start = (0,21,-5e-16)
  Subdivisions = 0
  expr: .End.x = 0 mm
  expr: .End.y = <<Line>>.End.y
  expr: .End.z = <<Line>>.End.z
  expr: .Start.x = 0 mm
  expr: .Start.y = <<Line>>.Start.y
  expr: .Start.z = <<Line>>.Start.z
FEATURE [Sketcher::SketchObject] Sketch024
  ExternalGeometry = -> [Line001]
  FullyConstrained = true
  MapMode = 7
  Placement = pos=(162.217,21,-1.8e-15) rot=(0.847961,-0.39253,-0.356205;1.82987rad)
  Support = -> [Line]
  sketch-geometry (3):
    g0: ArcOfCircle CenterX=-2.5 CenterY=2.80137 CenterZ=0 NormalX=0 NormalY=0 NormalZ=1 AngleXU=0 Radius=2.5 StartAngle=4.59882 EndAngle=6.28319
    g1: LineSegment StartX=-2.78332 StartY=0.317476 StartZ=0 EndX=0 EndY=7.1e-15 EndZ=0
    g2: LineSegment StartX=0 StartY=7.1e-15 StartZ=0 EndX=0 EndY=2.80137 EndZ=0
  constraints (8):
    c: Tangent(g0,g-3) = 1.5708
    c: Coincident(g1,g0)
    c: Coincident(g1,g-3)
    c: Coincident(g2,g1)
    c: Tangent(g2,g0) = -1.5708
    c: PointOnObject(g0,g-2)
    c: Radius(g0) = 2.5
    c: Distance(g1) = 2.80137  'length'
FEATURE [Sketcher::SketchObject] Sketch025
  ExternalGeometry = -> [Line]
  FullyConstrained = true
  MapMode = 7
  Placement = pos=(162.217,21,0) rot=(0.57735,0.57735,0.57735;2.0944rad)
  Support = -> [Line001]
  sketch-geometry (3):
    g0: ArcOfCircle CenterX=2.5 CenterY=2.90386 CenterZ=0 NormalX=0 NormalY=0 NormalZ=1 AngleXU=0 Radius=2.5 StartAngle=3.14159 EndAngle=4.86158
    g1: LineSegment StartX=2.84e-14 StartY=-5e-16 StartZ=0 EndX=0 EndY=2.90386 EndZ=0
    g2: LineSegment StartX=2.84e-14 StartY=-5e-16 StartZ=0 EndX=2.8716 EndY=0.431629 EndZ=0
  constraints (7):
    c: PointOnObject(g0,g-3)
    c: PointOnObject(g0,g-2)
    c: Coincident(g1,g-3)
    c: Coincident(g2,g1)
    c: Tangent(g2,g0) = -1.5708
    c: Tangent(g1,g0) = 1.5708
    c: Radius(g0) = 2.5
FEATURE [Sketcher::SketchObject] Sketch023  label="sink_base_sketch"
  ExternalGeometry = -> [Line,Sketch025,Sketch024,Line001]
  FullyConstrained = true
  MapMode = 5
  Placement = pos=(0,21,0) rot=(1,0,0;0.149193rad)
  Support = -> [Local_CS001]
  sketch-geometry (4):
    g0: LineSegment StartX=-161.299 StartY=2.90386 StartZ=0 EndX=161.299 EndY=2.90386 EndZ=0
    g1: LineSegment StartX=161.299 StartY=2.90386 StartZ=0 EndX=314.701 EndY=134.553 EndZ=0
    g2: LineSegment StartX=314.701 StartY=134.553 StartZ=0 EndX=-314.701 EndY=134.553 EndZ=0
    g3: LineSegment StartX=-314.701 StartY=134.553 StartZ=0 EndX=-161.299 EndY=2.90386 EndZ=0
  constraints (13):
    c: Coincident(g0,g1)
    c: Coincident(g1,g2)
    c: Coincident(g2,g3)
    c: Coincident(g3,g0)
    c: PointOnObject(g-4,g0)
    c: PointOnObject(g-5,g1)
    c: Parallel(g1,g-3)
    c: Horizontal(g1,g-3)
    c: Distance(g1) = 202.148  'side_length'
    c: Symmetric(g0,g0,g-2)
    c: Symmetric(g1,g2,g-2)
    c: Distance(g0) = 322.598  'front_length'
    c: Distance(g2) = 629.402  'end'
FEATURE [PartDesign::FeaturePython] BaseBend005  # WARN: FeaturePython — macro-defined, semantics opaque (R4)
  BendSide = 0
  BendSketch = -> Sketch023
  MidPlane = false
  Reverse = false
  length = 100
  radius = 2
  thickness = 0.5
FEATURE [Sketcher::SketchObject] Sketch026
  ExternalGeometry = -> [Sketch025]
  FullyConstrained = true
  MapMode = 5
  Placement = pos=(0,0,0) rot=(0.57735,0.57735,0.57735;2.0944rad)
  Support = -> [YZ_Plane010]
  sketch-geometry (4):
    g0: ArcOfCircle CenterX=23.5 CenterY=2.90386 CenterZ=0 NormalX=0 NormalY=0 NormalZ=1 AngleXU=0 Radius=2.5 StartAngle=3.14159 EndAngle=4.86158
    g1: LineSegment StartX=23.8716 StartY=0.431629 StartZ=0 EndX=23.7973 EndY=0.926074 EndZ=0
    g2: ArcOfCircle CenterX=23.5 CenterY=2.90386 CenterZ=0 NormalX=0 NormalY=0 NormalZ=1 AngleXU=0 Radius=2 StartAngle=3.14159 EndAngle=4.86158
    g3: LineSegment StartX=21 StartY=2.90386 StartZ=0 EndX=21.5 EndY=2.90386 EndZ=0
  constraints (10):
    c: Coincident(g2,g0)
    c: Coincident(g2,g1)
    c: Perpendicular(g0,g1)
    c: Coincident(g3,g0)
    c: Coincident(g3,g2)
    c: Horizontal(g3)
    c: DistanceX(g3,g3) = 0.5
    c: Coincident(g0,g-3)
    c: Tangent(g0,g-3) = -1.5708
    c: Coincident(g1,g0)
FEATURE [PartDesign::Pad] Pad002
  BaseFeature = -> BaseBend005
  Direction = (1,0,0)
  Length = 322.598
  Length2 = 10
  Midplane = true
  Profile = -> Sketch026
  ReferenceAxis = -> Sketch026 [N_Axis]
  Type = 0
  expr: Length = <<sink_base_sketch>>.Constraints.front_length
FEATURE [Sketcher::SketchObject] Sketch027
  AttachmentOffset = pos=(0,0,-21) rot=(0,0,1;0rad)
  ExternalGeometry = -> [Sketch025]
  FullyConstrained = true
  MapMode = 5
  Placement = pos=(0,21,-4.7e-15) rot=(1,0,0;1.5708rad)
  Support = -> [XZ_Plane010]
  expr: .AttachmentOffset.Base.z = -<<base_sketch>>.Constraints.offset
  expr: Constraints[10] = <<sink_base_sketch>>.Constraints.front_length
  sketch-geometry (4):
    g0: LineSegment StartX=-161.299 StartY=2.90386 StartZ=0 EndX=161.299 EndY=2.90386 EndZ=0
    g1: LineSegment StartX=161.299 StartY=2.90386 StartZ=0 EndX=161.299 EndY=80 EndZ=0
    g2: LineSegment StartX=161.299 StartY=80 StartZ=0 EndX=-161.299 EndY=80 EndZ=0
    g3: LineSegment StartX=-161.299 StartY=80 StartZ=0 EndX=-161.299 EndY=2.90386 EndZ=0
  constraints (11):
    c: Coincident(g0,g1)
    c: Coincident(g1,g2)
    c: Coincident(g2,g3)
    c: Coincident(g3,g0)
    c: Horizontal(g2)
    c: Vertical(g1)
    c: Vertical(g3)
    c: Horizontal(g0,g-3)
    c: DistanceY(g1) = 80
    c: Symmetric(g0,g0,g-2)
    c: DistanceX(g0,g0) = 322.598
FEATURE [PartDesign::Pad] Pad003
  BaseFeature = -> Pad002
  Direction = (0,-1,2e-16)
  Length = 0.5
  Length2 = 10
  Profile = -> Sketch027
  ReferenceAxis = -> Sketch027 [N_Axis]
  Reversed = true
  Type = 0
FEATURE [Sketcher::SketchObject] Sketch028
  ExternalGeometry = -> [Sketch024]
  FullyConstrained = true
  MapMode = 7
  Placement = pos=(163.124,21.7694,0.115643) rot=(0.847961,-0.39253,-0.356205;1.82987rad)
  Support = -> [Line,Sketch023]
  sketch-geometry (4):
    g0: ArcOfCircle CenterX=-2.5 CenterY=2.80137 CenterZ=0 NormalX=0 NormalY=0 NormalZ=1 AngleXU=0 Radius=2 StartAngle=4.59882 EndAngle=6.28319
    g1: ArcOfCircle CenterX=-2.5 CenterY=2.80137 CenterZ=0 NormalX=0 NormalY=0 NormalZ=1 AngleXU=0 Radius=2.5 StartAngle=4.59882 EndAngle=6.28319
    g2: LineSegment StartX=-2.78332 StartY=0.317476 StartZ=0 EndX=-2.72666 EndY=0.814255 EndZ=0
    g3: LineSegment StartX=-0.5 StartY=2.80137 StartZ=0 EndX=-1.42e-14 EndY=2.80137 EndZ=0
  constraints (10):
    c: Coincident(g0,g-3)
    c: Coincident(g1,g-3)
    c: Tangent(g1,g-3) = -1.5708
    c: Coincident(g2,g1)
    c: Coincident(g2,g0)
    c: Coincident(g3,g0)
    c: Coincident(g3,g1)
    c: Perpendicular(g1,g3)
    c: Perpendicular(g1,g2)
    c: Distance(g2) = 0.5
FEATURE [PartDesign::Pad] Pad004
  BaseFeature = -> Pad003
  Direction = (-0.75886,-0.64402,-0.0968023)
  Length = 202.148
  Length2 = 10
  Profile = -> Sketch028
  ReferenceAxis = -> Sketch028 [N_Axis]
  Reversed = true
  Type = 0
  expr: Length = <<sink_base_sketch>>.Constraints.side_length
FEATURE [PartDesign::Line] DatumLine
  AttacherType = Attacher::AttachEngineLine
  Length = 20
  MapMode = 16
  Placement = pos=(0,0,0) rot=(0,0,1;3.14159rad)
  ResizeMode = 0
  Support = -> [Z_Axis010]
FEATURE [Sketcher::SketchObject] Sketch029
  AttachmentOffset = pos=(0,0,0) rot=(0,1,0;1.5708rad)
  ExternalGeometry = -> [Line,Sketch028]
  FullyConstrained = true
  MapMode = 7
  Placement = pos=(162.217,21,0) rot=(0.887503,0.325836,0.325836;1.68986rad)
  Support = -> [Binder013]
  expr: Constraints[9] = <<sink_base_sketch>>.Constraints.side_length
  sketch-geometry (4):
    g0: LineSegment StartX=0.917845 StartY=2.90386 StartZ=0 EndX=0.917845 EndY=80 EndZ=0
    g1: LineSegment StartX=0.917845 StartY=80 StartZ=0 EndX=202.116 EndY=80 EndZ=0
    g2: LineSegment StartX=202.116 StartY=80 StartZ=0 EndX=202.116 EndY=22.4722 EndZ=0
    g3: LineSegment StartX=0.917845 StartY=2.90386 StartZ=0 EndX=202.116 EndY=22.4722 EndZ=0
  constraints (11):
    c: Coincident(g-4,g0)
    c: Vertical(g0)
    c: Coincident(g0,g1)
    c: Horizontal(g1)
    c: Coincident(g1,g2)
    c: Vertical(g2)
    c: Coincident(g3,g0)
    c: Coincident(g3,g2)
    c: Parallel(g3,g-3)
    c: Distance(g3) = 202.148
    c: DistanceY(g0) = 80
FEATURE [PartDesign::Pad] Pad005
  BaseFeature = -> Pad004
  Direction = (0.647059,-0.76244,0)
  Length = 0.5
  Length2 = 10
  Profile = -> Sketch029
  ReferenceAxis = -> Sketch029 [N_Axis]
  Reversed = true
  Type = 0
FEATURE [Part::Mirroring] Part__Mirroring008  label="Sketch028 (Mirror #9)"
  Base = (0,0,0)
  Normal = (1,0,0)
  Source = -> Sketch028
FEATURE [PartDesign::Pad] Pad006
  BaseFeature = -> Pad005
  Direction = (0.75886,-0.64402,-0.0968023)
  Length = 202.148
  Length2 = 10
  Profile = -> Part__Mirroring008
  Reversed = true
  Type = 0
  expr: Length = <<sink_base_sketch>>.Constraints.side_length
FEATURE [Part::Mirroring] Part__Mirroring009  label="Sketch029 (Mirror #10)"
  Base = (0,0,0)
  Normal = (1,0,0)
  Source = -> Sketch029
FEATURE [PartDesign::Pad] Pad007
  BaseFeature = -> Pad006
  Direction = (0.647059,0.76244,1e-16)
  Length = 0.5
  Length2 = 10
  Profile = -> Part__Mirroring009
  Type = 0
FEATURE [Sketcher::SketchObject] Sketch030
  ExternalGeometry = -> [Sketch023]
  FullyConstrained = true
  MapMode = 5
  Placement = pos=(0,0,0) rot=(0.57735,0.57735,0.57735;2.0944rad)
  Support = -> [YZ_Plane010]
  sketch-geometry (13):
    g0: ArcOfCircle CenterX=154.356 CenterY=18.0222 CenterZ=0 NormalX=0 NormalY=0 NormalZ=1 AngleXU=0 Radius=2 StartAngle=1.5708 EndAngle=1.71999
    g1: ArcOfCircle CenterX=154.356 CenterY=18.0222 CenterZ=0 NormalX=0 NormalY=0 NormalZ=1 AngleXU=0 Radius=2.5 StartAngle=1.5708 EndAngle=1.71999
    g2: ArcOfCircle CenterX=156.059 CenterY=18.0222 CenterZ=0 NormalX=0 NormalY=0 NormalZ=1 AngleXU=0 Radius=2 StartAngle=1.032e-13 EndAngle=1.5708
    g3: ArcOfCircle CenterX=156.059 CenterY=18.0222 CenterZ=0 NormalX=0 NormalY=0 NormalZ=1 AngleXU=0 Radius=2.5 StartAngle=8.21e-14 EndAngle=1.5708
    g4: LineSegment StartX=158.059 StartY=10.5222 StartZ=0 EndX=158.559 EndY=10.5222 EndZ=0
    g5: LineSegment StartX=158.559 StartY=10.5222 StartZ=0 EndX=158.559 EndY=18.0222 EndZ=0
    g6: LineSegment StartX=158.559 StartY=18.0222 StartZ=0 EndX=158.059 EndY=18.0222 EndZ=0
    g7: LineSegment StartX=158.059 StartY=18.0222 StartZ=0 EndX=158.059 EndY=10.5222 EndZ=0
    g8: LineSegment StartX=154.356 StartY=20.0222 StartZ=0 EndX=156.059 EndY=20.0222 EndZ=0
    g9: LineSegment StartX=156.059 StartY=20.0222 StartZ=0 EndX=156.059 EndY=20.5222 EndZ=0
    g10: LineSegment StartX=156.059 StartY=20.5222 StartZ=0 EndX=154.356 EndY=20.5222 EndZ=0
    g11: LineSegment StartX=154.356 StartY=20.5222 StartZ=0 EndX=154.356 EndY=20.0222 EndZ=0
    g12: LineSegment StartX=154.059 StartY=20 StartZ=0 EndX=153.984 EndY=20.4944 EndZ=0
  constraints (35):
    c: Coincident(g1,g0)
    c: Coincident(g3,g2)
    c: Coincident(g4,g5)
    c: Coincident(g5,g6)
    c: Coincident(g6,g7)
    c: Coincident(g7,g4)
    c: Horizontal(g4)
    c: Horizontal(g6)
    c: Vertical(g5)
    c: Vertical(g7)
    c: Coincident(g5,g3)
    c: Coincident(g6,g2)
    c: Coincident(g8,g9)
    c: Coincident(g9,g10)
    c: Coincident(g10,g11)
    c: Horizontal(g8)
    c: Horizontal(g10)
    c: Vertical(g9)
    c: Vertical(g11)
    c: Coincident(g9,g3)
    c: Coincident(g1,g10)
    c: Coincident(g12,g1)
    c: Perpendicular(g0,g12)
    c: PointOnObject(g2,g6)
    c: Equal(g2,g0)
    c: Tangent(g2,g8) = 1.5708
    c: DistanceY(g11,g11) = 0.5
    c: Radius(g2) = 2
    c: Tangent(g8,g0) = 1.5708
    c: Coincident(g11,g0)
    c: DistanceX(g0,g2) = 4
    c: DistanceY(g4,g3) = 10
    c: Coincident(g12,g-3)
    c: Coincident(g0,g12)
    c: Perpendicular(g-3,g12)
FEATURE [PartDesign::Pad] Pad008
  BaseFeature = -> Pad007
  Direction = (1,0,0)
  Length = 629.402
  Length2 = 10
  Midplane = true
  Profile = -> Sketch030
  ReferenceAxis = -> Sketch030 [N_Axis]
  Type = 0
  expr: Length = <<sink_base_sketch>>.Constraints.end
FEATURE [Sketcher::SketchObject] Sketch031
  ExternalGeometry = -> [Sketch023]
  FullyConstrained = true
  MapMode = 5
  Placement = pos=(0,21,0) rot=(1,0,0;0.149193rad)
  Support = -> [Local_CS001]
  sketch-geometry (5):
    g0: ArcOfCircle CenterX=161.299 CenterY=2.90386 CenterZ=0 NormalX=0 NormalY=0 NormalZ=1 AngleXU=0 Radius=10 StartAngle=0.709236 EndAngle=3.14159
    g1: LineSegment StartX=151.299 StartY=2.90386 StartZ=0 EndX=151.299 EndY=0 EndZ=0
    g2: LineSegment StartX=151.299 StartY=0 StartZ=0 EndX=162.374 EndY=0 EndZ=0
    g3: LineSegment StartX=162.374 StartY=0 StartZ=0 EndX=170.779 EndY=7.21278 EndZ=0
    g4: LineSegment StartX=170.779 StartY=7.21278 StartZ=0 EndX=168.888 EndY=9.4164 EndZ=0
  constraints (14):
    c: Coincident(g0,g-3)
    c: PointOnObject(g0,g-3)
    c: Radius(g0) = 10
    c: Tangent(g0,g1) = -1.5708
    c: Coincident(g1,g2)
    c: PointOnObject(g2,g-1)
    c: Horizontal(g2)
    c: Coincident(g2,g3)
    c: Coincident(g3,g4)
    c: Coincident(g4,g0)
    c: Vertical(g1)
    c: Perpendicular(g-3,g4)
    c: Equal(g4,g1)
    c: Perpendicular(g4,g3)
FEATURE [Sketcher::SketchObject] Sketch032
  ExternalGeometry = -> [Sketch029,Sketch031]
  FullyConstrained = true
  MapMode = 2
  Placement = pos=(162.217,21,0) rot=(0.887503,0.325836,0.325836;1.68986rad)
  Support = -> [Sketch029]
  sketch-geometry (9):
    g0: LineSegment StartX=1.15829 StartY=0.431629 StartZ=0 EndX=11.1113 EndY=1.39965 EndZ=0
    g1: LineSegment StartX=1.15829 StartY=0.431629 StartZ=0 EndX=0.917845 EndY=2.90386 EndZ=0
    g2: LineSegment StartX=11.1113 StartY=1.39965 StartZ=0 EndX=10.8709 EndY=3.87188 EndZ=0
    g3: LineSegment StartX=0.917845 StartY=2.90386 StartZ=0 EndX=0.917845 EndY=17.046 EndZ=0
    g4: ArcOfCircle CenterX=5.91784 CenterY=75 CenterZ=0 NormalX=0 NormalY=0 NormalZ=1 AngleXU=0 Radius=5 StartAngle=1.5708 EndAngle=3.14159
    g5: LineSegment StartX=0.917845 StartY=75 StartZ=0 EndX=0.917845 EndY=80 EndZ=0
    g6: LineSegment StartX=0.917845 StartY=80 StartZ=0 EndX=5.91784 EndY=80 EndZ=0
    g7: ArcOfCircle CenterX=0.917845 CenterY=2.90386 CenterZ=0 NormalX=0 NormalY=0 NormalZ=1 AngleXU=0 Radius=10 StartAngle=0.0969541 EndAngle=1.23096
    g8: ArcOfCircle CenterX=5.91784 CenterY=17.046 CenterZ=0 NormalX=0 NormalY=0 NormalZ=1 AngleXU=0 Radius=5 StartAngle=3.14159 EndAngle=4.37255
  constraints (23):
    c: Coincident(g0,g-4)
    c: PointOnObject(g0,g-4)
    c: Parallel(g0,g-5)
    c: Coincident(g1,g0)
    c: Coincident(g1,g-5)
    c: Coincident(g2,g0)
    c: PointOnObject(g2,g-5)
    c: Perpendicular(g0,g2)
    c: Coincident(g3,g1)
    c: Vertical(g3)
    c: Coincident(g7,g1)
    c: Coincident(g7,g2)
    c: Coincident(g5,g6)
    c: Coincident(g6,g4)
    c: Horizontal(g6)
    c: Tangent(g6,g4)
    c: Coincident(g5,g-3)
    c: Vertical(g5)
    c: Tangent(g4,g5) = 1.5708
    c: Radius(g4) = 5
    c: Tangent(g8,g7) = 1.5708
    c: Tangent(g8,g3) = 1.5708
    c: Radius(g8) = 5
FEATURE [PartDesign::Pocket] Pocket005
  BaseFeature = -> Pad008
  Direction = (0,0.14864,-0.988891)
  Length = 5
  Length2 = 5
  Midplane = true
  Profile = -> Sketch031
  ReferenceAxis = -> Sketch031 [N_Axis]
  Type = 0
FEATURE [PartDesign::Pocket] Pocket006
  BaseFeature = -> Pocket005
  Direction = (-0.647059,0.76244,0)
  Length = 2.80137
  Length2 = 5
  Profile = -> Sketch032
  ReferenceAxis = -> Sketch032 [N_Axis]
  Type = 0
  expr: Length = <<Sketch024>>.Constraints.length
FEATURE [Sketcher::SketchObject] Sketch033
  ExternalGeometry = -> [Sketch031,Sketch027]
  FullyConstrained = true
  MapMode = 2
  Placement = pos=(0,21,-4.7e-15) rot=(1,0,0;1.5708rad)
  Support = -> [Sketch027]
  sketch-geometry (8):
    g0: LineSegment StartX=161.299 StartY=0.431629 StartZ=0 EndX=151.299 EndY=0.431629 EndZ=0
    g1: LineSegment StartX=151.299 StartY=0.431629 StartZ=0 EndX=151.299 EndY=2.90386 EndZ=0
    g2: LineSegment StartX=161.299 StartY=0.431629 StartZ=0 EndX=161.299 EndY=17.046 EndZ=0
    g3: ArcOfCircle CenterX=156.299 CenterY=75 CenterZ=0 NormalX=0 NormalY=0 NormalZ=1 AngleXU=0 Radius=5 StartAngle=2.4e-15 EndAngle=1.5708
    g4: LineSegment StartX=156.299 StartY=80 StartZ=0 EndX=161.299 EndY=80 EndZ=0
    g5: LineSegment StartX=161.299 StartY=80 StartZ=0 EndX=161.299 EndY=75 EndZ=0
    g6: ArcOfCircle CenterX=161.299 CenterY=2.90386 CenterZ=0 NormalX=0 NormalY=0 NormalZ=1 AngleXU=0 Radius=10 StartAngle=1.91063 EndAngle=3.14159
    g7: ArcOfCircle CenterX=156.299 CenterY=17.046 CenterZ=0 NormalX=0 NormalY=0 NormalZ=1 AngleXU=0 Radius=5 StartAngle=5.05223 EndAngle=6.28319
  constraints (19):
    c: Coincident(g0,g-3)
    c: PointOnObject(g0,g-3)
    c: Horizontal(g0)
    c: PointOnObject(g2,g-4)
    c: Tangent(g1,g6) = 1.5708
    c: Vertical(g1)
    c: Coincident(g1,g0)
    c: Coincident(g2,g0)
    c: PointOnObject(g3,g-4)
    c: Coincident(g4,g5)
    c: Tangent(g5,g3) = 1.5708
    c: Tangent(g3,g4) = 1.5708
    c: Horizontal(g4)
    c: Coincident(g4,g-4)
    c: Radius(g3) = 5
    c: Tangent(g7,g6) = 1.5708
    c: Tangent(g7,g2) = -1.5708
    c: Radius(g7) = 5
    c: Coincident(g6,g-4)
FEATURE [PartDesign::Pocket] Pocket007
  BaseFeature = -> Pocket006
  Direction = (0,1,-2e-16)
  Length = 0.7
  Length2 = 5
  Profile = -> Sketch033
  ReferenceAxis = -> Sketch033 [N_Axis]
  Refine = true
  Type = 0
FEATURE [Sketcher::SketchObject] Sketch034
  ExternalGeometry = -> [Sketch029]
  FullyConstrained = false
  MapMode = 2
  Placement = pos=(162.217,21,0) rot=(0.887503,0.325836,0.325836;1.68986rad)
  Support = -> [Sketch029]
  sketch-geometry (6):
    g0: ArcOfCircle CenterX=206.072 CenterY=77 CenterZ=0 NormalX=0 NormalY=0 NormalZ=1 AngleXU=0 Radius=3 StartAngle=5.06802 EndAngle=7.85398
    g1: ArcOfCircle CenterX=204.116 CenterY=25.6809 CenterZ=0 NormalX=0 NormalY=0 NormalZ=1 AngleXU=0 Radius=3 StartAngle=4.80934 EndAngle=6.28319
    g2: LineSegment StartX=202.116 StartY=22.4722 StartZ=0 EndX=204.407 EndY=22.695 EndZ=0
    g3: LineSegment StartX=202.116 StartY=80 StartZ=0 EndX=206.072 EndY=80 EndZ=0
    g4: LineSegment StartX=202.116 StartY=80 StartZ=0 EndX=202.116 EndY=22.4722 EndZ=0
    g5: LineSegment StartX=207.116 StartY=25.6809 StartZ=0 EndX=207.116 EndY=74.1877 EndZ=0
  constraints (14):
    c: Coincident(g2,g-4)
    c: Coincident(g3,g-3)
    c: Coincident(g4,g3)
    c: Coincident(g4,g2)
    c: Coincident(g5,g0)
    c: Equal(g0,g1)
    c: Radius(g0) = 3
    c: Tangent(g5,g1) = -1.5708
    c: Parallel(g2,g-4)
    c: Tangent(g2,g1) = -1.5708
    c: Vertical(g5)
    c: Tangent(g3,g0) = 1.5708
    c: Horizontal(g3)
    c: DistanceX(g2,g1) = 5
FEATURE [PartDesign::Pad] Pad009
  BaseFeature = -> Pocket007
  Direction = (0.647059,-0.76244,0)
  Length = 0.5
  Length2 = 10
  Profile = -> Sketch034
  ReferenceAxis = -> Sketch034 [N_Axis]
  Reversed = true
  Type = 0
FEATURE [PartDesign::Fillet] Fillet
  Base = -> Pad009 [Edge88]
  BaseFeature = -> Pad009
  Radius = 2
  SupportTransform = false
  UseAllEdges = false
FEATURE [PartDesign::Mirrored] Mirrored004
  BaseFeature = -> Fillet
  MirrorPlane = -> YZ_Plane010
  Originals = -> [Pocket005,Pocket006,Pocket007,Pad009,Fillet]
  Refine = true
FEATURE [Sketcher::SketchObject] Sketch035
  ExternalGeometry = -> [Sketch023]
  FullyConstrained = true
  MapMode = 5
  Placement = pos=(0,21,0) rot=(1,0,0;0.149193rad)
  Support = -> [Local_CS001]
  sketch-geometry (4):
    g0: ArcOfCircle CenterX=0 CenterY=2.90386 CenterZ=0 NormalX=0 NormalY=0 NormalZ=1 AngleXU=0 Radius=10 StartAngle=0 EndAngle=3.14159
    g1: LineSegment StartX=-10 StartY=2.90386 StartZ=0 EndX=-10 EndY=0 EndZ=0
    g2: LineSegment StartX=-10 StartY=0 StartZ=0 EndX=10 EndY=0 EndZ=0
    g3: LineSegment StartX=10 StartY=0 StartZ=0 EndX=10 EndY=2.90386 EndZ=0
  constraints (13):
    c: PointOnObject(g0,g-3)
    c: PointOnObject(g0,g-3)
    c: PointOnObject(g0,g-3)
    c: PointOnObject(g0,g-2)
    c: Coincident(g1,g0)
    c: PointOnObject(g1,g-1)
    c: Vertical(g1)
    c: Coincident(g2,g1)
    c: PointOnObject(g2,g-1)
    c: Coincident(g3,g2)
    c: Coincident(g3,g0)
    c: Vertical(g3)
    c: Radius(g0) = 10
FEATURE [Sketcher::SketchObject] Sketch036
  AttachmentOffset = pos=(0,0,-14) rot=(0,0,1;0rad)
  ExternalGeometry = -> [Sketch025,Sketch035]
  FullyConstrained = true
  MapMode = 5
  Placement = pos=(0,14,-3.1e-15) rot=(1,0,0;1.5708rad)
  Support = -> [XZ_Plane010]
  sketch-geometry (4):
    g0: ArcOfCircle CenterX=0 CenterY=2.90386 CenterZ=0 NormalX=0 NormalY=0 NormalZ=1 AngleXU=0 Radius=10 StartAngle=0 EndAngle=3.14159
    g1: LineSegment StartX=10 StartY=5.1e-15 StartZ=0 EndX=10 EndY=2.90386 EndZ=0
    g2: LineSegment StartX=10 StartY=5.1e-15 StartZ=0 EndX=-10 EndY=0 EndZ=0
    g3: LineSegment StartX=-10 StartY=0 StartZ=0 EndX=-10 EndY=2.90386 EndZ=0
  constraints (10):
    c: PointOnObject(g0,g-2)
    c: Horizontal(g0,g-3)
    c: Coincident(g1,g-4)
    c: Vertical(g1)
    c: Tangent(g1,g0) = -1.5708
    c: Coincident(g1,g2)
    c: PointOnObject(g2,g-1)
    c: Coincident(g2,g3)
    c: Tangent(g3,g0) = 1.5708
    c: Vertical(g3)
FEATURE [PartDesign::Boolean] Boolean004
  BaseFeature = -> Mirrored004
  Group = -> [Compound012]
  Type = 1
FEATURE [PartDesign::Body] Body007  label="sink_ss_material_0.30ansi"
  Group = -> [Line001,Line,Binder013,DatumPoint,Local_CS001,Sketch023,Line002,Sketch024,Sketch025,BaseBend005,Sketch026,Pad002,Sketch027,Pad003,Sketch028,Pad004,DatumLine,Sketch029,Pad005,Part__Mirroring008,Pad006,Part__Mirroring009,Pad007,Sketch030,Pad008,Sketch031,Sketch032,Pocket005,Pocket006,Sketch033,Pocket007,Sketch034,Pad009,Fillet,Mirrored004,Sketch035,Sketch036,Boolean004]
  Origin = -> Origin010
  Tip = -> Boolean004
COMPONENT P8 — recipe-attached ("bar_part", modeled in this document).
Construction recipe (the document's own serialized feature program — sketch geometry with constraints, then the solid features built on it; lengths are millimeters unless a unit is written):

FEATURE [PartDesign::SubShapeBinder] Binder014
  BindCopyOnChange = 0
  BindMode = 0
  ClaimChildren = true
  Context = -> Part003 [Body009.Binder014.]
  Fuse = false
  MakeFace = true
  OffsetFill = false
  OffsetIntersection = false
  OffsetJoinType = 0
  OffsetOpenResult = false
  PartialLoad = false
  Relative = true
  Support = -> [Sketch039]
  _Version = 2
FEATURE [PartDesign::SubShapeBinder] Binder015
  BindCopyOnChange = 0
  BindMode = 0
  ClaimChildren = true
  Context = -> Part003 [Body009.Binder015.]
  Fuse = false
  MakeFace = true
  OffsetFill = false
  OffsetIntersection = false
  OffsetJoinType = 0
  OffsetOpenResult = false
  PartialLoad = false
  Relative = true
  Support = -> [Connect005]
  _Version = 2
FEATURE [Sketcher::SketchObject] Sketch042
  FullyConstrained = true
  MapMode = 5
  Placement = pos=(0,0,0) rot=(0.57735,0.57735,0.57735;2.0944rad)
  Support = -> [YZ_Plane013]
  sketch-geometry (4):
    g0: ArcOfCircle CenterX=4 CenterY=4 CenterZ=0 NormalX=0 NormalY=0 NormalZ=1 AngleXU=0 Radius=4 StartAngle=3.14159 EndAngle=4.71239
    g1: ArcOfCircle CenterX=4 CenterY=4 CenterZ=0 NormalX=0 NormalY=0 NormalZ=1 AngleXU=0 Radius=2 StartAngle=3.14159 EndAngle=4.71239
    g2: LineSegment StartX=0 StartY=4 StartZ=0 EndX=2 EndY=4 EndZ=0
    g3: LineSegment StartX=4 StartY=0 StartZ=0 EndX=4 EndY=2 EndZ=0
  constraints (11):
    c: Coincident(g1,g0)
    c: Coincident(g2,g0)
    c: Coincident(g2,g1)
    c: Coincident(g3,g0)
    c: Coincident(g3,g1)
    c: Perpendicular(g1,g3)
    c: Perpendicular(g1,g2)
    c: Tangent(g0,g-1) = -1.5708
    c: Tangent(g0,g-2) = 1.5708
    c: Radius(g1) = 2
    c: DistanceY(g3,g3) = 2
FEATURE [Sketcher::SketchObject] Sketch043
  FullyConstrained = true
  MapMode = 5
  Support = -> [XY_Plane013]
  sketch-geometry (10):
    g0: LineSegment StartX=-34 StartY=4 StartZ=0 EndX=-34 EndY=65 EndZ=0
    g1: LineSegment StartX=-27 StartY=72 StartZ=0 EndX=27 EndY=72 EndZ=0
    g2: LineSegment StartX=34 StartY=65 StartZ=0 EndX=34 EndY=4 EndZ=0
    g3: LineSegment StartX=34 StartY=4 StartZ=0 EndX=-34 EndY=4 EndZ=0
    g4: GeomPoint X=0 Y=38 Z=0
    g5: ArcOfCircle CenterX=27 CenterY=65 CenterZ=0 NormalX=0 NormalY=0 NormalZ=1 AngleXU=0 Radius=7 StartAngle=0 EndAngle=1.5708
    g6: GeomPoint X=34 Y=72 Z=0
    g7: ArcOfCircle CenterX=-27 CenterY=65 CenterZ=0 NormalX=0 NormalY=0 NormalZ=1 AngleXU=0 Radius=7 StartAngle=1.5708 EndAngle=3.14159
    g8: GeomPoint X=-34 Y=72 Z=0
    g9: LineSegment StartX=34 StartY=4 StartZ=0 EndX=34 EndY=72 EndZ=0
  constraints (23):
    c: Coincident(g2,g3)
    c: Coincident(g3,g0)
    c: Horizontal(g1)
    c: Horizontal(g3)
    c: Vertical(g0)
    c: Vertical(g2)
    c: Symmetric(g6,g0,g4)
    c: PointOnObject(g4,g-2)
    c: DistanceY(g2) = 4
    c: DistanceX(g3,g3) = 68  'width'
    c: PointOnObject(g6,g1)
    c: PointOnObject(g6,g2)
    c: Tangent(g1,g5) = 1.5708
    c: Tangent(g2,g5) = 1.5708
    c: PointOnObject(g8,g0)
    c: PointOnObject(g8,g1)
    c: Tangent(g0,g7) = 1.5708
    c: Tangent(g1,g7) = 1.5708
    c: Equal(g5,g7)
    c: Radius(g5) = 7
    c: Coincident(g9,g2)
    c: Coincident(g9,g6)
    c: Equal(g9,g3)
FEATURE [PartDesign::Pad] Pad011
  Direction = (1,0,0)
  Length = 68
  Length2 = 10
  Midplane = true
  Placement = pos=(0,0,0) rot=(0.57735,0.57735,0.57735;2.0944rad)
  Profile = -> Sketch042
  ReferenceAxis = -> Sketch042 [N_Axis]
  Type = 0
  expr: Length = <<Sketch043>>.Constraints.width
FEATURE [PartDesign::Pad] Pad012
  BaseFeature = -> Pad011
  Direction = (0,0,1)
  Length = 2
  Length2 = 10
  Placement = pos=(0,0,0) rot=(0.57735,0.57735,0.57735;2.0944rad)
  Profile = -> Sketch043
  ReferenceAxis = -> Sketch043 [N_Axis]
  Type = 0
FEATURE [Sketcher::SketchObject] Sketch044
  ExternalGeometry = -> [Sketch043]
  FullyConstrained = true
  MapMode = 5
  Placement = pos=(0,0,0) rot=(1,0,0;1.5708rad)
  Support = -> [XZ_Plane013]
  sketch-geometry (9):
    g0: LineSegment StartX=34 StartY=59 StartZ=0 EndX=34 EndY=4 EndZ=0
    g1: LineSegment StartX=34 StartY=4 StartZ=0 EndX=-34 EndY=4 EndZ=0
    g2: LineSegment StartX=-34 StartY=4 StartZ=0 EndX=-34 EndY=59 EndZ=0
    g3: GeomPoint X=0 Y=35 Z=0
    g4: ArcOfCircle CenterX=-27 CenterY=59 CenterZ=0 NormalX=0 NormalY=0 NormalZ=1 AngleXU=0 Radius=7 StartAngle=1.5708 EndAngle=3.14159
    g5: GeomPoint X=-34 Y=66 Z=0
    g6: ArcOfCircle CenterX=27 CenterY=59 CenterZ=0 NormalX=0 NormalY=0 NormalZ=1 AngleXU=0 Radius=7 StartAngle=0 EndAngle=1.5708
    g7: GeomPoint X=34 Y=66 Z=0
    g8: LineSegment StartX=-27 StartY=66 StartZ=0 EndX=27 EndY=66 EndZ=0
  constraints (21):
    c: Coincident(g0,g1)
    c: Coincident(g1,g2)
    c: Horizontal(g1)
    c: Vertical(g0)
    c: Vertical(g2)
    c: Symmetric(g1,g7,g3)
    c: PointOnObject(g3,g-2)
    c: DistanceY(g1) = 4
    c: Vertical(g0,g-3)
    c: DistanceY(g5) = 66
    c: PointOnObject(g5,g2)
    c: PointOnObject(g7,g0)
    c: Equal(g4,g6)
    c: Radius(g4) = 7
    c: Tangent(g6,g8) = 1.5708
    c: Tangent(g6,g0) = 1.5708
    c: Tangent(g8,g4) = 1.5708
    c: Tangent(g2,g4) = 1.5708
    c: Horizontal(g8)
    c: PointOnObject(g5,g8)
    c: PointOnObject(g7,g8)
FEATURE [PartDesign::Pad] Pad013
  BaseFeature = -> Pad012
  Direction = (0,-1,2e-16)
  Length = 2
  Length2 = 10
  Placement = pos=(0,0,0) rot=(0.57735,0.57735,0.57735;2.0944rad)
  Profile = -> Sketch044
  ReferenceAxis = -> Sketch044 [N_Axis]
  Reversed = true
  Type = 0
FEATURE [PartDesign::Pad] Pad010
  Direction = (0,0,1)
  Length = 1305.01
  Length2 = 10
  Profile = -> Binder015
  Type = 0
  expr: Length = <<length>>.Length - 6 mm
FEATURE [PartDesign::Fillet] Fillet001
  Base = -> Pad010 [Edge48]
  BaseFeature = -> Pad010
  Radius = 2
  SupportTransform = false
  UseAllEdges = false
FEATURE [PartDesign::Mirrored] Mirrored005
  MirrorPlane = -> YZ_Plane012
FEATURE [PartDesign::Plane] DatumPlane002
  AttachmentOffset = pos=(0,0,652.505) rot=(0,0,1;0rad)
  Length = 79.6619
  MapMode = 5
  Placement = pos=(0,0,652.505) rot=(0,0,1;0rad)
  ResizeMode = 0
  Support = -> [XY_Plane012]
  Width = 61.6619
  expr: .AttachmentOffset.Base.z = Pad010.Length / 2
FEATURE [PartDesign::Mirrored] Mirrored006
  MirrorPlane = -> DatumPlane002
FEATURE [Sketcher::SketchObject] Sketch045
  ExternalGeometry = -> [Binder015]
  FullyConstrained = true
  MapMode = 5
  Support = -> [XY_Plane012]
  sketch-geometry (12):
    g0: LineSegment StartX=0 StartY=14 StartZ=0 EndX=16 EndY=14 EndZ=0
    g1: LineSegment StartX=16 StartY=14 StartZ=0 EndX=16 EndY=12 EndZ=0
    g2: LineSegment StartX=16 StartY=12 StartZ=0 EndX=0 EndY=12 EndZ=0
    g3: LineSegment StartX=0 StartY=12 StartZ=0 EndX=0 EndY=14 EndZ=0
    g4: LineSegment StartX=18 StartY=4 StartZ=0 EndX=20 EndY=4 EndZ=0
    g5: LineSegment StartX=20 StartY=4 StartZ=0 EndX=20 EndY=12 EndZ=0
    g6: LineSegment StartX=20 StartY=12 StartZ=0 EndX=18 EndY=12 EndZ=0
    g7: LineSegment StartX=18 StartY=12 StartZ=0 EndX=18 EndY=4 EndZ=0
    g8: LineSegment StartX=22 StartY=2 StartZ=0 EndX=34 EndY=2 EndZ=0
    g9: LineSegment StartX=34 StartY=2 StartZ=0 EndX=34 EndY=0 EndZ=0
    g10: LineSegment StartX=34 StartY=0 StartZ=0 EndX=22 EndY=0 EndZ=0
    g11: LineSegment StartX=22 StartY=0 StartZ=0 EndX=22 EndY=2 EndZ=0
  constraints (30):
    c: Coincident(g0,g1)
    c: Coincident(g1,g2)
    c: Coincident(g2,g3)
    c: Coincident(g3,g0)
    c: Horizontal(g2)
    c: Vertical(g1)
    c: Vertical(g3)
    c: Coincident(g0,g-5)
    c: Coincident(g4,g5)
    c: Coincident(g5,g6)
    c: Coincident(g6,g7)
    c: Coincident(g7,g4)
    c: Horizontal(g4)
    c: Horizontal(g6)
    c: Vertical(g5)
    c: Coincident(g4,g-4)
    c: Coincident(g8,g9)
    c: Coincident(g9,g10)
    c: Coincident(g10,g11)
    c: Coincident(g11,g8)
    c: Horizontal(g10)
    c: Vertical(g9)
    c: Vertical(g11)
    c: Coincident(g8,g-3)
    c: PointOnObject(g9,g-1)
    c: Coincident(g8,g-3)
    c: Equal(g11,g4)
    c: Equal(g4,g1)
    c: Coincident(g0,g-5)
    c: Coincident(g6,g-4)
FEATURE [PartDesign::Pocket] Pocket008
  BaseFeature = -> Fillet001
  Direction = (0,0,-1)
  Length = 5
  Length2 = 5
  Profile = -> Sketch045
  ReferenceAxis = -> Sketch045 [N_Axis]
  Type = 0
FEATURE [PartDesign::MultiTransform] MultiTransform
  BaseFeature = -> Pocket008
  Originals = -> [Fillet001,Pocket008]
  Refine = true
  Transformations = -> [Mirrored005,Mirrored006]
FEATURE [PartDesign::Boolean] Boolean005
  BaseFeature = -> MultiTransform
  Group = -> [Compound013]
  Type = 1
FEATURE [PartDesign::Body] Body009  label="bar_material_0.50ansi"
  Group = -> [Binder014,Binder015,Pad010,Fillet001,Pocket008,MultiTransform,Mirrored005,DatumPlane002,Mirrored006,Sketch045,Boolean005]
  Origin = -> Origin012
  Tip = -> Boolean005
FEATURE [PartDesign::Boolean] Boolean006
  BaseFeature = -> Pad013
  Group = -> [Compound014]
  Type = 1
FEATURE [PartDesign::Body] Body010  label="bar_fix_material_0.50ansi"
  Group = -> [Sketch042,Sketch043,Pad011,Pad012,Sketch044,Pad013,Boolean006]
  Origin = -> Origin013
  Tip = -> Boolean006
COMPONENT P9 — recipe-attached ("door", modeled in this document).
Construction recipe (the document's own serialized feature program — sketch geometry with constraints, then the solid features built on it; lengths are millimeters unless a unit is written):

FEATURE [PartDesign::SubShapeBinder] Binder026
  BindCopyOnChange = 0
  BindMode = 0
  ClaimChildren = true
  Context = -> Part004 [Body016.Binder026.]
  Fuse = false
  MakeFace = true
  OffsetFill = false
  OffsetIntersection = false
  OffsetJoinType = 0
  OffsetOpenResult = false
  PartialLoad = false
  Relative = false
  Support = -> [Sketch063]
  _Version = 2
  expr: Support = <<door_plexiglas_BaseSketch>>._self
FEATURE [PartDesign::FeaturePython] BaseBend010  # WARN: FeaturePython — macro-defined, semantics opaque (R4)
  BendSide = 1
  BendSketch = -> Binder026
  MidPlane = false
  Reverse = false
  length = 100
  radius = 1
  thickness = 4
FEATURE [PartDesign::Body] Body016  label="door_plexiglass"
  Group = -> [BaseBend010,Binder026]
  Origin = -> Origin020
  Tip = -> BaseBend010
FEATURE [PartDesign::Body] Body017  label="door_fix"
  Origin = -> Origin022
PROVENANCE & LICENSES
A FreeCAD (.FCStd) document from a public repository crawl; recipes are the document's own serialized feature recipes (and, for linked parts, companion documents' recipes).
License: as declared in the source repository (recorded in the dataset sidecar).
